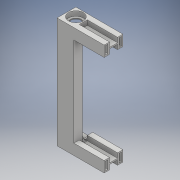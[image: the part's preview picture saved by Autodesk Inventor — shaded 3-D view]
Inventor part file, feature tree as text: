
AUTODESK INVENTOR PART (.ipt)
format: ipt  version: 2018 (Build 220112000, 112)  size: 260,608 bytes
history: native  units: mm
features: extrude x9, sketch x9, fillet x3
ambient origin geometry x8: Origin, YZ Plane, XZ Plane, XY Plane, X Axis, Y Axis, Z Axis, Center Point
bodies: Solid1 (feature_tree)
feature tree (21):
  extrude  "Extrusion1"  Depth=165.0mm
  extrude  "Extrusion2"  Depth=8.5mm
  extrude  "Extrusion3"  Depth=25.0mm TaperAngle=0.0deg
  extrude  "Extrusion4"  Depth=25.0mm
  extrude  "Extrusion5"  Depth=7.1mm
  extrude  "Extrusion6"  Depth=7.1mm TaperAngle=0.0deg
  fillet  "Fillet1"  Radius=5.0mm
  extrude  "Extrusion7"  Depth=10.0mm TaperAngle=0.0deg
  fillet  "Fillet2"  Radius=2.0mm
  extrude  "Extrusion8"  Depth=8.0mm
  extrude  "Extrusion9"  Depth=16.0mm
  fillet  "Fillet3"  Radius=8.0mm
  sketch  "Sketch1"  dims[d0=25.0mm d1=165.0mm]
  sketch  "Sketch2"  dims[d2=3.0mm d3=0.0mm d4=8.5mm]
  sketch  "Sketch3"  dims[d5=8.5mm d6=25.0mm d7=0.0mm]
  sketch  "Sketch4"  dims[d8=25.0mm d9=22.0mm]
  sketch  "Sketch5"  dims[d10=7.1mm d11=0.0mm d12=15.5mm]
  sketch  "Sketch6"  dims[d13=165.0mm d14=0.0mm d15=7.1mm d16=0.0mm d17=5.0mm]
  sketch  "Sketch7"  dims[d18=5.0mm d19=10.0mm d20=0.0mm d21=2.0mm]
  sketch  "Sketch8"  dims[d22=16.0mm d23=8.0mm]
  sketch  "Sketch9"  dims[d24=16.0mm d25=16.0mm d26=8.0mm d27=45.0mm d28=0.0mm d29=6.0mm d30=12.25mm d31=3.5mm d32=12.25mm d33=3.5mm d34=12.25mm d35=12.25mm d36=3.5mm d37=40.0mm d38=0.0mm d39=1.0mm d40=2.0mm d41=8.0mm d42=1.0mm d43=2.0mm d44=12.0mm d45=0.0mm d46=6.0mm]
